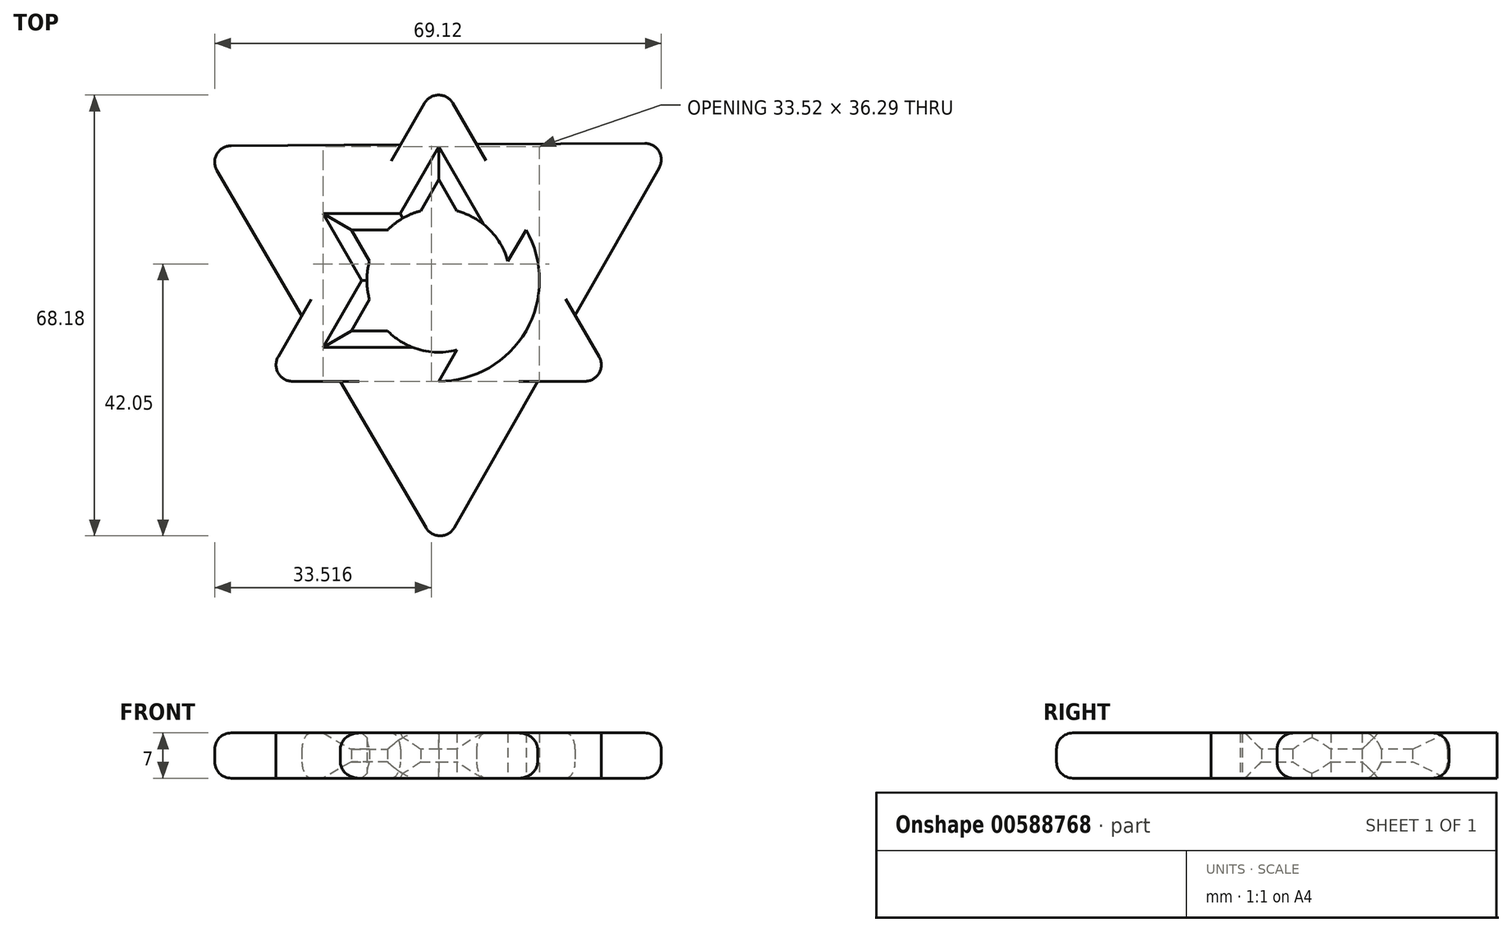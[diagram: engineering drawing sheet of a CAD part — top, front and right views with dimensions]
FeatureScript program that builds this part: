
annotation { "Feature Type Name" : "Feature", "Feature Type Description" : "" }
export const myFeature = defineFeature(function(context is Context, id is Id, definition is map)
    precondition{}
    {
        {
            var Q0;
            Q0=qCreatedBy(makeId("Top.planeOp"),FACE);
            var sketch = newSketch(context, id + "F0", { "sketchPlane" : qUnion([Q0])});
            skCircle(sketch, "E0", {"center": v(0, 0) * mm, "radius": 11.11 * mm});
            skCircle(sketch, "E1", {"center": v(0, 0) * mm, "radius": 15.6 * mm});
            skCircle(sketch, "E2.cCircle", {"center": v(0, 0) * mm, "radius": 15.6 * mm, "construction": true});
            skLineSegment(sketch, "E2.0", {"start": v(0, -15.6) * mm, "end": v(-13.52, 7.8) * mm});
            skLineSegment(sketch, "E2.1", {"start": v(-13.52, 7.8) * mm, "end": v(13.52, 7.8) * mm});
            skLineSegment(sketch, "E2.2", {"start": v(13.52, 7.8) * mm, "end": v(0, -15.6) * mm});
            skLineSegment(sketch, "E3.MirrorCS", {"start": v(-27.03, -15.6) * mm, "end": v(0, -15.6) * mm});
            skLineSegment(sketch, "E4.MirrorCS", {"start": v(-13.52, 7.8) * mm, "end": v(-27.03, -15.6) * mm});
            skLineSegment(sketch, "E5.MirrorCS", {"start": v(0, 31.21) * mm, "end": v(-13.52, 7.8) * mm});
            skLineSegment(sketch, "E6.MirrorCS", {"start": v(13.52, 7.8) * mm, "end": v(0, 31.21) * mm});
            skLineSegment(sketch, "E7.MirrorCS", {"start": v(0, -15.6) * mm, "end": v(27.03, -15.6) * mm});
            skLineSegment(sketch, "E8.MirrorCS", {"start": v(27.03, -15.6) * mm, "end": v(13.52, 7.8) * mm});
            skCircle(sketch, "E9.cCircle", {"center": v(0, 0) * mm, "radius": 42.05 * mm, "construction": true});
            skLineSegment(sketch, "E9.0", {"start": v(36.3, 21.24) * mm, "end": v(0.25, -42.05) * mm});
            skLineSegment(sketch, "E9.1", {"start": v(0.25, -42.05) * mm, "end": v(-36.54, 20.8) * mm});
            skLineSegment(sketch, "E9.2", {"start": v(-36.54, 20.8) * mm, "end": v(36.3, 21.24) * mm});
            skLineSegment(sketch, "E10.0", {"start": v(13.52, -7.8) * mm, "end": v(-13.52, -7.8) * mm});
            skLineSegment(sketch, "E10.1", {"start": v(-13.52, -7.8) * mm, "end": v(0, 15.6) * mm});
            skLineSegment(sketch, "E10.2", {"start": v(0, 15.6) * mm, "end": v(13.52, -7.8) * mm});
            skSolve(sketch);
        }
        {
            var Q0;
            Q0 = qSketchRegion(id + "F0", true);
            var Q1;
            {var subQ0=sQuery(id+"F0.wireOp",EDGE,"E2.0");var subQ1=sQuery(id+"F0.wireOp",EDGE,"E0");var subQ2=makeQuery(id+"F0.imprint","INTERSECT",VERTEX,{"disambiguationData":[OD(0.0)],"derivedFrom":[subQ1,subQ0]});Q1=makeQuery(id+"F0.imprint","IMPRINT",FACE,{"disambiguationData":[TD([[makeQuery(id+"F0.imprint","IMPRINT",EDGE,{"disambiguationData":[TD([[subQ2,-1.0]])],"derivedFrom":subQ1}),-1.0]])]});}
            var Q2;
            {var subQ0=sQuery(id+"F0.wireOp",EDGE,"E2.1");var subQ1=sQuery(id+"F0.wireOp",EDGE,"E0");var subQ2=makeQuery(id+"F0.imprint","INTERSECT",VERTEX,{"disambiguationData":[OD(0.0)],"derivedFrom":[subQ1,subQ0]});Q2=makeQuery(id+"F0.imprint","IMPRINT",FACE,{"disambiguationData":[TD([[makeQuery(id+"F0.imprint","IMPRINT",EDGE,{"disambiguationData":[TD([[subQ2,-1.0]])],"derivedFrom":subQ1}),-1.0]])]});}
            var Q3;
            {var subQ0=sQuery(id+"F0.wireOp",EDGE,"E2.2");var subQ1=sQuery(id+"F0.wireOp",EDGE,"E0");var subQ2=makeQuery(id+"F0.imprint","INTERSECT",VERTEX,{"disambiguationData":[OD(1.0)],"derivedFrom":[subQ1,subQ0]});Q3=makeQuery(id+"F0.imprint","IMPRINT",FACE,{"disambiguationData":[TD([[makeQuery(id+"F0.imprint","IMPRINT",EDGE,{"disambiguationData":[TD([[subQ2,-1.0]])],"derivedFrom":subQ1}),-1.0]])]});}
            var Q4;
            {var subQ0=sQuery(id+"F0.wireOp",EDGE,"E10.0");var subQ1=sQuery(id+"F0.wireOp",EDGE,"E0");var subQ2=makeQuery(id+"F0.imprint","INTERSECT",VERTEX,{"disambiguationData":[OD(0.0)],"derivedFrom":[subQ1,subQ0]});Q4=makeQuery(id+"F0.imprint","IMPRINT",FACE,{"disambiguationData":[TD([[makeQuery(id+"F0.imprint","IMPRINT",EDGE,{"disambiguationData":[TD([[subQ2,-1.0]])],"derivedFrom":subQ1}),-1.0]])]});}
            var Q5;
            {var subQ0=sQuery(id+"F0.wireOp",EDGE,"E2.2");var subQ1=sQuery(id+"F0.wireOp",EDGE,"E0");var subQ2=makeQuery(id+"F0.imprint","INTERSECT",VERTEX,{"disambiguationData":[OD(0.0)],"derivedFrom":[subQ1,subQ0]});Q5=makeQuery(id+"F0.imprint","IMPRINT",FACE,{"disambiguationData":[TD([[makeQuery(id+"F0.imprint","IMPRINT",EDGE,{"disambiguationData":[TD([[subQ2,1.0]])],"derivedFrom":subQ1}),-1.0]])]});}
            var Q6;
            {var subQ0=sQuery(id+"F0.wireOp",EDGE,"E10.1");var subQ1=sQuery(id+"F0.wireOp",EDGE,"E0");var subQ2=makeQuery(id+"F0.imprint","INTERSECT",VERTEX,{"disambiguationData":[OD(0.0)],"derivedFrom":[subQ1,subQ0]});Q6=makeQuery(id+"F0.imprint","IMPRINT",FACE,{"disambiguationData":[TD([[makeQuery(id+"F0.imprint","IMPRINT",EDGE,{"disambiguationData":[TD([[subQ2,-1.0]])],"derivedFrom":subQ1}),-1.0]])]});}
            extrude(context, id + "F1", {"entities" : qUnion([Q0, Q1, Q2, Q3, Q4, Q5, Q6]), "depth" : 7 * mm, "offsetDistance" : 25.4 * mm});
        }
        {
            var Q0;
            {var subQ0=sQuery(id+"F0.wireOp",EDGE,"E2.1");Q0=makeQuery(id+"F1.opExtrude","CAP_EDGE",EDGE,{"disambiguationData":[OSD([subQ0]),TDD([makeQuery(id+"F0.imprint","IMPRINT",EDGE,{"disambiguationData":[TD([[makeQuery(id+"F0.imprint","INTERSECT",VERTEX,{"disambiguationData":[OD(1.0)],"derivedFrom":[sQuery(id+"F0.wireOp",EDGE,"E0"),subQ0]}),1.0]])],"derivedFrom":subQ0})])],"isStart":false});}
            var Q1;
            {var subQ0=sQuery(id+"F0.wireOp",EDGE,"E2.1");Q1=makeQuery(id+"F1.opExtrude","CAP_EDGE",EDGE,{"disambiguationData":[OSD([subQ0]),TDD([makeQuery(id+"F0.imprint","IMPRINT",EDGE,{"disambiguationData":[TD([[makeQuery(id+"F0.imprint","INTERSECT",VERTEX,{"disambiguationData":[OD(1.0)],"derivedFrom":[sQuery(id+"F0.wireOp",EDGE,"E0"),subQ0]}),1.0]])],"derivedFrom":subQ0})])],"isStart":true});}
            var Q2;
            {var subQ0=sQuery(id+"F0.wireOp",EDGE,"E2.0");Q2=makeQuery(id+"F1.opExtrude","CAP_EDGE",EDGE,{"disambiguationData":[OSD([subQ0]),TDD([makeQuery(id+"F0.imprint","IMPRINT",EDGE,{"disambiguationData":[TD([[makeQuery(id+"F0.imprint","INTERSECT",VERTEX,{"disambiguationData":[OD(0.0)],"derivedFrom":[sQuery(id+"F0.wireOp",EDGE,"E0"),subQ0]}),-1.0]])],"derivedFrom":subQ0})])],"isStart":true});}
            var Q3;
            {var subQ0=sQuery(id+"F0.wireOp",EDGE,"E10.0");Q3=makeQuery(id+"F1.opExtrude","CAP_EDGE",EDGE,{"disambiguationData":[OSD([subQ0]),TDD([makeQuery(id+"F0.imprint","IMPRINT",EDGE,{"disambiguationData":[TD([[makeQuery(id+"F0.imprint","INTERSECT",VERTEX,{"disambiguationData":[OD(0.0)],"derivedFrom":[sQuery(id+"F0.wireOp",EDGE,"E0"),subQ0]}),-1.0]])],"derivedFrom":subQ0})])],"isStart":true});}
            var Q4;
            {var subQ0=sQuery(id+"F0.wireOp",EDGE,"E10.1");Q4=makeQuery(id+"F1.opExtrude","CAP_EDGE",EDGE,{"disambiguationData":[OSD([subQ0]),TDD([makeQuery(id+"F0.imprint","IMPRINT",EDGE,{"disambiguationData":[TD([[makeQuery(id+"F0.imprint","INTERSECT",VERTEX,{"disambiguationData":[OD(1.0)],"derivedFrom":[sQuery(id+"F0.wireOp",EDGE,"E0"),subQ0]}),1.0]])],"derivedFrom":subQ0})])],"isStart":true});}
            var Q5;
            {var subQ0=sQuery(id+"F0.wireOp",EDGE,"E2.0");Q5=makeQuery(id+"F1.opExtrude","CAP_EDGE",EDGE,{"disambiguationData":[OSD([subQ0]),TDD([makeQuery(id+"F0.imprint","IMPRINT",EDGE,{"disambiguationData":[TD([[makeQuery(id+"F0.imprint","INTERSECT",VERTEX,{"disambiguationData":[OD(1.0)],"derivedFrom":[sQuery(id+"F0.wireOp",EDGE,"E0"),subQ0]}),1.0]])],"derivedFrom":subQ0})])],"isStart":true});}
            var Q6;
            {var subQ0=sQuery(id+"F0.wireOp",EDGE,"E2.2");Q6=makeQuery(id+"F1.opExtrude","CAP_EDGE",EDGE,{"disambiguationData":[OSD([subQ0]),TDD([makeQuery(id+"F0.imprint","IMPRINT",EDGE,{"disambiguationData":[TD([[makeQuery(id+"F0.imprint","INTERSECT",VERTEX,{"disambiguationData":[OD(1.0)],"derivedFrom":[sQuery(id+"F0.wireOp",EDGE,"E0"),subQ0]}),-1.0]])],"derivedFrom":subQ0})])],"isStart":true});}
            var Q7;
            {var subQ0=sQuery(id+"F0.wireOp",EDGE,"E10.0");Q7=makeQuery(id+"F1.opExtrude","CAP_EDGE",EDGE,{"disambiguationData":[OSD([subQ0]),TDD([makeQuery(id+"F0.imprint","IMPRINT",EDGE,{"disambiguationData":[TD([[makeQuery(id+"F0.imprint","INTERSECT",VERTEX,{"disambiguationData":[OD(1.0)],"derivedFrom":[sQuery(id+"F0.wireOp",EDGE,"E0"),subQ0]}),1.0]])],"derivedFrom":subQ0})])],"isStart":true});}
            var Q8;
            {var subQ0=sQuery(id+"F0.wireOp",EDGE,"E10.2");Q8=makeQuery(id+"F1.opExtrude","CAP_EDGE",EDGE,{"disambiguationData":[OSD([subQ0]),TDD([makeQuery(id+"F0.imprint","IMPRINT",EDGE,{"disambiguationData":[TD([[makeQuery(id+"F0.imprint","INTERSECT",VERTEX,{"disambiguationData":[OD(1.0)],"derivedFrom":[sQuery(id+"F0.wireOp",EDGE,"E0"),subQ0]}),-1.0]])],"derivedFrom":subQ0})])],"isStart":true});}
            var Q9;
            {var subQ0=sQuery(id+"F0.wireOp",EDGE,"E2.2");Q9=makeQuery(id+"F1.opExtrude","CAP_EDGE",EDGE,{"disambiguationData":[OSD([subQ0]),TDD([makeQuery(id+"F0.imprint","IMPRINT",EDGE,{"disambiguationData":[TD([[makeQuery(id+"F0.imprint","INTERSECT",VERTEX,{"disambiguationData":[OD(0.0)],"derivedFrom":[sQuery(id+"F0.wireOp",EDGE,"E0"),subQ0]}),1.0]])],"derivedFrom":subQ0})])],"isStart":true});}
            var Q10;
            {var subQ0=sQuery(id+"F0.wireOp",EDGE,"E2.1");Q10=makeQuery(id+"F1.opExtrude","CAP_EDGE",EDGE,{"disambiguationData":[OSD([subQ0]),TDD([makeQuery(id+"F0.imprint","IMPRINT",EDGE,{"disambiguationData":[TD([[makeQuery(id+"F0.imprint","INTERSECT",VERTEX,{"disambiguationData":[OD(0.0)],"derivedFrom":[sQuery(id+"F0.wireOp",EDGE,"E0"),subQ0]}),-1.0]])],"derivedFrom":subQ0})])],"isStart":true});}
            var Q11;
            {var subQ0=sQuery(id+"F0.wireOp",EDGE,"E10.2");Q11=makeQuery(id+"F1.opExtrude","CAP_EDGE",EDGE,{"disambiguationData":[OSD([subQ0]),TDD([makeQuery(id+"F0.imprint","IMPRINT",EDGE,{"disambiguationData":[TD([[makeQuery(id+"F0.imprint","INTERSECT",VERTEX,{"disambiguationData":[OD(0.0)],"derivedFrom":[sQuery(id+"F0.wireOp",EDGE,"E0"),subQ0]}),1.0]])],"derivedFrom":subQ0})])],"isStart":true});}
            var Q12;
            {var subQ0=sQuery(id+"F0.wireOp",EDGE,"E10.1");Q12=makeQuery(id+"F1.opExtrude","CAP_EDGE",EDGE,{"disambiguationData":[OSD([subQ0]),TDD([makeQuery(id+"F0.imprint","IMPRINT",EDGE,{"disambiguationData":[TD([[makeQuery(id+"F0.imprint","INTERSECT",VERTEX,{"disambiguationData":[OD(0.0)],"derivedFrom":[sQuery(id+"F0.wireOp",EDGE,"E0"),subQ0]}),-1.0]])],"derivedFrom":subQ0})])],"isStart":true});}
            var Q13;
            {var subQ0=sQuery(id+"F0.wireOp",EDGE,"E10.1");Q13=makeQuery(id+"F1.opExtrude","CAP_EDGE",EDGE,{"disambiguationData":[OSD([subQ0]),TDD([makeQuery(id+"F0.imprint","IMPRINT",EDGE,{"disambiguationData":[TD([[makeQuery(id+"F0.imprint","INTERSECT",VERTEX,{"disambiguationData":[OD(0.0)],"derivedFrom":[sQuery(id+"F0.wireOp",EDGE,"E0"),subQ0]}),-1.0]])],"derivedFrom":subQ0})])],"isStart":false});}
            var Q14;
            {var subQ0=sQuery(id+"F0.wireOp",EDGE,"E10.2");Q14=makeQuery(id+"F1.opExtrude","CAP_EDGE",EDGE,{"disambiguationData":[OSD([subQ0]),TDD([makeQuery(id+"F0.imprint","IMPRINT",EDGE,{"disambiguationData":[TD([[makeQuery(id+"F0.imprint","INTERSECT",VERTEX,{"disambiguationData":[OD(0.0)],"derivedFrom":[sQuery(id+"F0.wireOp",EDGE,"E0"),subQ0]}),1.0]])],"derivedFrom":subQ0})])],"isStart":false});}
            var Q15;
            {var subQ0=sQuery(id+"F0.wireOp",EDGE,"E2.1");Q15=makeQuery(id+"F1.opExtrude","CAP_EDGE",EDGE,{"disambiguationData":[OSD([subQ0]),TDD([makeQuery(id+"F0.imprint","IMPRINT",EDGE,{"disambiguationData":[TD([[makeQuery(id+"F0.imprint","INTERSECT",VERTEX,{"disambiguationData":[OD(0.0)],"derivedFrom":[sQuery(id+"F0.wireOp",EDGE,"E0"),subQ0]}),-1.0]])],"derivedFrom":subQ0})])],"isStart":false});}
            var Q16;
            {var subQ0=sQuery(id+"F0.wireOp",EDGE,"E2.2");Q16=makeQuery(id+"F1.opExtrude","CAP_EDGE",EDGE,{"disambiguationData":[OSD([subQ0]),TDD([makeQuery(id+"F0.imprint","IMPRINT",EDGE,{"disambiguationData":[TD([[makeQuery(id+"F0.imprint","INTERSECT",VERTEX,{"disambiguationData":[OD(0.0)],"derivedFrom":[sQuery(id+"F0.wireOp",EDGE,"E0"),subQ0]}),1.0]])],"derivedFrom":subQ0})])],"isStart":false});}
            var Q17;
            {var subQ0=sQuery(id+"F0.wireOp",EDGE,"E10.2");Q17=makeQuery(id+"F1.opExtrude","CAP_EDGE",EDGE,{"disambiguationData":[OSD([subQ0]),TDD([makeQuery(id+"F0.imprint","IMPRINT",EDGE,{"disambiguationData":[TD([[makeQuery(id+"F0.imprint","INTERSECT",VERTEX,{"disambiguationData":[OD(1.0)],"derivedFrom":[sQuery(id+"F0.wireOp",EDGE,"E0"),subQ0]}),-1.0]])],"derivedFrom":subQ0})])],"isStart":false});}
            var Q18;
            {var subQ0=sQuery(id+"F0.wireOp",EDGE,"E10.0");Q18=makeQuery(id+"F1.opExtrude","CAP_EDGE",EDGE,{"disambiguationData":[OSD([subQ0]),TDD([makeQuery(id+"F0.imprint","IMPRINT",EDGE,{"disambiguationData":[TD([[makeQuery(id+"F0.imprint","INTERSECT",VERTEX,{"disambiguationData":[OD(1.0)],"derivedFrom":[sQuery(id+"F0.wireOp",EDGE,"E0"),subQ0]}),1.0]])],"derivedFrom":subQ0})])],"isStart":false});}
            var Q19;
            {var subQ0=sQuery(id+"F0.wireOp",EDGE,"E2.2");Q19=makeQuery(id+"F1.opExtrude","CAP_EDGE",EDGE,{"disambiguationData":[OSD([subQ0]),TDD([makeQuery(id+"F0.imprint","IMPRINT",EDGE,{"disambiguationData":[TD([[makeQuery(id+"F0.imprint","INTERSECT",VERTEX,{"disambiguationData":[OD(1.0)],"derivedFrom":[sQuery(id+"F0.wireOp",EDGE,"E0"),subQ0]}),-1.0]])],"derivedFrom":subQ0})])],"isStart":false});}
            var Q20;
            {var subQ0=sQuery(id+"F0.wireOp",EDGE,"E2.0");Q20=makeQuery(id+"F1.opExtrude","CAP_EDGE",EDGE,{"disambiguationData":[OSD([subQ0]),TDD([makeQuery(id+"F0.imprint","IMPRINT",EDGE,{"disambiguationData":[TD([[makeQuery(id+"F0.imprint","INTERSECT",VERTEX,{"disambiguationData":[OD(1.0)],"derivedFrom":[sQuery(id+"F0.wireOp",EDGE,"E0"),subQ0]}),1.0]])],"derivedFrom":subQ0})])],"isStart":false});}
            var Q21;
            {var subQ0=sQuery(id+"F0.wireOp",EDGE,"E10.0");Q21=makeQuery(id+"F1.opExtrude","CAP_EDGE",EDGE,{"disambiguationData":[OSD([subQ0]),TDD([makeQuery(id+"F0.imprint","IMPRINT",EDGE,{"disambiguationData":[TD([[makeQuery(id+"F0.imprint","INTERSECT",VERTEX,{"disambiguationData":[OD(0.0)],"derivedFrom":[sQuery(id+"F0.wireOp",EDGE,"E0"),subQ0]}),-1.0]])],"derivedFrom":subQ0})])],"isStart":false});}
            var Q22;
            {var subQ0=sQuery(id+"F0.wireOp",EDGE,"E10.1");Q22=makeQuery(id+"F1.opExtrude","CAP_EDGE",EDGE,{"disambiguationData":[OSD([subQ0]),TDD([makeQuery(id+"F0.imprint","IMPRINT",EDGE,{"disambiguationData":[TD([[makeQuery(id+"F0.imprint","INTERSECT",VERTEX,{"disambiguationData":[OD(1.0)],"derivedFrom":[sQuery(id+"F0.wireOp",EDGE,"E0"),subQ0]}),1.0]])],"derivedFrom":subQ0})])],"isStart":false});}
            var Q23;
            {var subQ0=sQuery(id+"F0.wireOp",EDGE,"E2.0");Q23=makeQuery(id+"F1.opExtrude","CAP_EDGE",EDGE,{"disambiguationData":[OSD([subQ0]),TDD([makeQuery(id+"F0.imprint","IMPRINT",EDGE,{"disambiguationData":[TD([[makeQuery(id+"F0.imprint","INTERSECT",VERTEX,{"disambiguationData":[OD(0.0)],"derivedFrom":[sQuery(id+"F0.wireOp",EDGE,"E0"),subQ0]}),-1.0]])],"derivedFrom":subQ0})])],"isStart":false});}
            chamfer(context, id + "F2", {"entities" : qUnion([Q0, Q1, Q2, Q3, Q4, Q5, Q6, Q7, Q8, Q9, Q10, Q11, Q12, Q13, Q14, Q15, Q16, Q17, Q18, Q19, Q20, Q21, Q22, Q23]), "width" : 2.54 * mm, "tangentPropagation" : true});
        }
        {
            var Q0;
            {var subQ0=sQuery(id+"F0.wireOp",EDGE,"E9.1");Q0=makeQuery(id+"F1.opExtrude","CAP_EDGE",EDGE,{"disambiguationData":[OSD([subQ0]),TDD([makeQuery(id+"F0.imprint","IMPRINT",EDGE,{"disambiguationData":[TD([[makeQuery(id+"F0.imprint","INTERSECT",VERTEX,{"derivedFrom":[subQ0,sQuery(id+"F0.wireOp",EDGE,"E9.2")]}),1.0]])],"derivedFrom":subQ0})])],"isStart":true});}
            var Q1;
            {var subQ0=sQuery(id+"F0.wireOp",EDGE,"E9.1");Q1=makeQuery(id+"F1.opExtrude","CAP_EDGE",EDGE,{"disambiguationData":[OSD([subQ0]),TDD([makeQuery(id+"F0.imprint","IMPRINT",EDGE,{"disambiguationData":[TD([[makeQuery(id+"F0.imprint","INTERSECT",VERTEX,{"derivedFrom":[subQ0,sQuery(id+"F0.wireOp",EDGE,"E9.2")]}),1.0]])],"derivedFrom":subQ0})])],"isStart":false});}
            var Q2;
            {var subQ0=sQuery(id+"F0.wireOp",EDGE,"E9.2");Q2=makeQuery(id+"F1.opExtrude","CAP_EDGE",EDGE,{"disambiguationData":[OSD([subQ0]),TDD([makeQuery(id+"F0.imprint","IMPRINT",EDGE,{"disambiguationData":[TD([[makeQuery(id+"F0.imprint","INTERSECT",VERTEX,{"derivedFrom":[sQuery(id+"F0.wireOp",EDGE,"E9.1"),subQ0]}),-1.0]])],"derivedFrom":subQ0})])],"isStart":false});}
            var Q3;
            {var subQ0=sQuery(id+"F0.wireOp",EDGE,"E9.2");Q3=makeQuery(id+"F1.opExtrude","CAP_EDGE",EDGE,{"disambiguationData":[OSD([subQ0]),TDD([makeQuery(id+"F0.imprint","IMPRINT",EDGE,{"disambiguationData":[TD([[makeQuery(id+"F0.imprint","INTERSECT",VERTEX,{"derivedFrom":[sQuery(id+"F0.wireOp",EDGE,"E9.1"),subQ0]}),-1.0]])],"derivedFrom":subQ0})])],"isStart":true});}
            var Q4;
            {var subQ0=sQuery(id+"F0.wireOp",EDGE,"E9.2");Q4=makeQuery(id+"F1.opExtrude","CAP_EDGE",EDGE,{"disambiguationData":[OSD([subQ0]),TDD([makeQuery(id+"F0.imprint","IMPRINT",EDGE,{"disambiguationData":[TD([[makeQuery(id+"F0.imprint","INTERSECT",VERTEX,{"derivedFrom":[sQuery(id+"F0.wireOp",EDGE,"E9.0"),subQ0]}),1.0]])],"derivedFrom":subQ0})])],"isStart":true});}
            var Q5;
            {var subQ0=sQuery(id+"F0.wireOp",EDGE,"E9.2");Q5=makeQuery(id+"F1.opExtrude","CAP_EDGE",EDGE,{"disambiguationData":[OSD([subQ0]),TDD([makeQuery(id+"F0.imprint","IMPRINT",EDGE,{"disambiguationData":[TD([[makeQuery(id+"F0.imprint","INTERSECT",VERTEX,{"derivedFrom":[sQuery(id+"F0.wireOp",EDGE,"E9.0"),subQ0]}),1.0]])],"derivedFrom":subQ0})])],"isStart":false});}
            var Q6;
            {var subQ0=sQuery(id+"F0.wireOp",EDGE,"E9.0");Q6=makeQuery(id+"F1.opExtrude","CAP_EDGE",EDGE,{"disambiguationData":[OSD([subQ0]),TDD([makeQuery(id+"F0.imprint","IMPRINT",EDGE,{"disambiguationData":[TD([[makeQuery(id+"F0.imprint","INTERSECT",VERTEX,{"derivedFrom":[subQ0,sQuery(id+"F0.wireOp",EDGE,"E9.2")]}),-1.0]])],"derivedFrom":subQ0})])],"isStart":false});}
            var Q7;
            {var subQ0=sQuery(id+"F0.wireOp",EDGE,"E9.0");Q7=makeQuery(id+"F1.opExtrude","CAP_EDGE",EDGE,{"disambiguationData":[OSD([subQ0]),TDD([makeQuery(id+"F0.imprint","IMPRINT",EDGE,{"disambiguationData":[TD([[makeQuery(id+"F0.imprint","INTERSECT",VERTEX,{"derivedFrom":[subQ0,sQuery(id+"F0.wireOp",EDGE,"E9.2")]}),-1.0]])],"derivedFrom":subQ0})])],"isStart":true});}
            var Q8;
            {var subQ0=sQuery(id+"F0.wireOp",EDGE,"E9.0");Q8=makeQuery(id+"F1.opExtrude","CAP_EDGE",EDGE,{"disambiguationData":[OSD([subQ0]),TDD([makeQuery(id+"F0.imprint","IMPRINT",EDGE,{"disambiguationData":[TD([[makeQuery(id+"F0.imprint","INTERSECT",VERTEX,{"derivedFrom":[subQ0,sQuery(id+"F0.wireOp",EDGE,"E9.1")]}),1.0]])],"derivedFrom":subQ0})])],"isStart":true});}
            var Q9;
            {var subQ0=sQuery(id+"F0.wireOp",EDGE,"E9.0");Q9=makeQuery(id+"F1.opExtrude","CAP_EDGE",EDGE,{"disambiguationData":[OSD([subQ0]),TDD([makeQuery(id+"F0.imprint","IMPRINT",EDGE,{"disambiguationData":[TD([[makeQuery(id+"F0.imprint","INTERSECT",VERTEX,{"derivedFrom":[subQ0,sQuery(id+"F0.wireOp",EDGE,"E9.1")]}),1.0]])],"derivedFrom":subQ0})])],"isStart":false});}
            var Q10;
            {var subQ0=sQuery(id+"F0.wireOp",EDGE,"E9.1");Q10=makeQuery(id+"F1.opExtrude","CAP_EDGE",EDGE,{"disambiguationData":[OSD([subQ0]),TDD([makeQuery(id+"F0.imprint","IMPRINT",EDGE,{"disambiguationData":[TD([[makeQuery(id+"F0.imprint","INTERSECT",VERTEX,{"derivedFrom":[sQuery(id+"F0.wireOp",EDGE,"E9.0"),subQ0]}),-1.0]])],"derivedFrom":subQ0})])],"isStart":false});}
            var Q11;
            {var subQ0=sQuery(id+"F0.wireOp",EDGE,"E9.1");Q11=makeQuery(id+"F1.opExtrude","CAP_EDGE",EDGE,{"disambiguationData":[OSD([subQ0]),TDD([makeQuery(id+"F0.imprint","IMPRINT",EDGE,{"disambiguationData":[TD([[makeQuery(id+"F0.imprint","INTERSECT",VERTEX,{"derivedFrom":[sQuery(id+"F0.wireOp",EDGE,"E9.0"),subQ0]}),-1.0]])],"derivedFrom":subQ0})])],"isStart":true});}
            fillet(context, id + "F3", {"entities" : qUnion([Q0, Q1, Q2, Q3, Q4, Q5, Q6, Q7, Q8, Q9, Q10, Q11]), "radius" : 2.54 * mm, "tangentPropagation" : true, "allowEdgeOverflow" : false});
        }
        {
            var Q0;
            {var subQ0=sQuery(id+"F0.wireOp",EDGE,"E9.2");var subQ1=sQuery(id+"F0.wireOp",EDGE,"E9.1");var subQ2=makeQuery(id+"F0.imprint","INTERSECT",VERTEX,{"derivedFrom":[subQ1,subQ0]});Q0=makeQuery(id+"F3.opFillet","BLEND_EDGE",EDGE,{"blendedFrom":[makeQuery(id+"F1.opExtrude","CAP_EDGE",EDGE,{"disambiguationData":[OSD([subQ1]),TDD([makeQuery(id+"F0.imprint","IMPRINT",EDGE,{"disambiguationData":[TD([[subQ2,1.0]])],"derivedFrom":subQ1})])],"isStart":false}),makeQuery(id+"F1.opExtrude","CAP_EDGE",EDGE,{"disambiguationData":[OSD([subQ0]),TDD([makeQuery(id+"F0.imprint","IMPRINT",EDGE,{"disambiguationData":[TD([[subQ2,-1.0]])],"derivedFrom":subQ0})])],"isStart":false})],"blendedInto":[]});}
            var Q1;
            {var subQ0=sQuery(id+"F0.wireOp",EDGE,"E9.2");var subQ1=sQuery(id+"F0.wireOp",EDGE,"E9.0");var subQ2=makeQuery(id+"F0.imprint","INTERSECT",VERTEX,{"derivedFrom":[subQ1,subQ0]});Q1=makeQuery(id+"F3.opFillet","BLEND_EDGE",EDGE,{"blendedFrom":[makeQuery(id+"F1.opExtrude","CAP_EDGE",EDGE,{"disambiguationData":[OSD([subQ1]),TDD([makeQuery(id+"F0.imprint","IMPRINT",EDGE,{"disambiguationData":[TD([[subQ2,-1.0]])],"derivedFrom":subQ1})])],"isStart":true}),makeQuery(id+"F1.opExtrude","CAP_EDGE",EDGE,{"disambiguationData":[OSD([subQ0]),TDD([makeQuery(id+"F0.imprint","IMPRINT",EDGE,{"disambiguationData":[TD([[subQ2,1.0]])],"derivedFrom":subQ0})])],"isStart":true})],"blendedInto":[]});}
            var Q2;
            {var subQ0=sQuery(id+"F0.wireOp",EDGE,"E9.1");var subQ1=sQuery(id+"F0.wireOp",EDGE,"E9.0");Q2=makeQuery(id+"F3.opFillet","BLEND_EDGE",EDGE,{"blendedFrom":[makeQuery(id+"F1.opExtrude","CAP_VERTEX",VERTEX,{"disambiguationData":[OSD([subQ1,subQ0])],"isStart":false}),makeQuery(id+"F1.opExtrude","SWEPT_EDGE",EDGE,{"disambiguationData":[OSD([subQ1,subQ0])]})],"blendedInto":[]});}
            var Q3;
            {var subQ0=sQuery(id+"F0.wireOp",EDGE,"E9.1");var subQ1=sQuery(id+"F0.wireOp",EDGE,"E9.0");var subQ2=makeQuery(id+"F0.imprint","INTERSECT",VERTEX,{"derivedFrom":[subQ1,subQ0]});Q3=makeQuery(id+"F3.opFillet","BLEND_EDGE",EDGE,{"blendedFrom":[makeQuery(id+"F1.opExtrude","CAP_EDGE",EDGE,{"disambiguationData":[OSD([subQ1]),TDD([makeQuery(id+"F0.imprint","IMPRINT",EDGE,{"disambiguationData":[TD([[subQ2,1.0]])],"derivedFrom":subQ1})])],"isStart":true}),makeQuery(id+"F1.opExtrude","CAP_EDGE",EDGE,{"disambiguationData":[OSD([subQ0]),TDD([makeQuery(id+"F0.imprint","IMPRINT",EDGE,{"disambiguationData":[TD([[subQ2,-1.0]])],"derivedFrom":subQ0})])],"isStart":true})],"blendedInto":[]});}
            fillet(context, id + "F4", {"entities" : qUnion([Q0, Q1, Q2, Q3]), "radius" : 2.54 * mm, "tangentPropagation" : true, "allowEdgeOverflow" : false});
        }
        {
            var Q0;
            Q0=makeQuery(id+"F1.opExtrude","SWEPT_EDGE",EDGE,{"disambiguationData":[OSD([sQuery(id+"F0.wireOp",EDGE,"E7.MirrorCS"),sQuery(id+"F0.wireOp",EDGE,"E8.MirrorCS")])]});
            var Q1;
            Q1=makeQuery(id+"F1.opExtrude","SWEPT_EDGE",EDGE,{"disambiguationData":[OSD([sQuery(id+"F0.wireOp",EDGE,"E3.MirrorCS"),sQuery(id+"F0.wireOp",EDGE,"E4.MirrorCS")])]});
            var Q2;
            Q2=makeQuery(id+"F1.opExtrude","SWEPT_EDGE",EDGE,{"disambiguationData":[OSD([sQuery(id+"F0.wireOp",EDGE,"E5.MirrorCS"),sQuery(id+"F0.wireOp",EDGE,"E6.MirrorCS")])]});
            fillet(context, id + "F5", {"entities" : qUnion([Q0, Q1, Q2]), "radius" : 2.54 * mm, "tangentPropagation" : true, "allowEdgeOverflow" : false});
        }
    });
